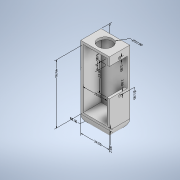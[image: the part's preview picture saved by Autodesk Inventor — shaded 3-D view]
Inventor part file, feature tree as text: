
AUTODESK INVENTOR PART (.ipt)
format: ipt  version: 2022.2 (Build 262287010, 287A)  size: 219,648 bytes
history: native  units: mm
features: other x14, extrude x8, sketch x8, fillet x1
ambient origin geometry x8: Origin, YZ Plane, XZ Plane, XY Plane, X Axis, Y Axis, Z Axis, Center Point
bodies: Solid1 (feature_tree)
feature tree (31):
  other  "Annotations"
  extrude  "Extrusion1"  Depth=24.0mm
  extrude  "Extrusion2"  Depth=2.0mm
  extrude  "Extrusion3"  Depth=15.0mm TaperAngle=0.0deg
  extrude  "Extrusion4"  Depth=2.0mm
  extrude  "Extrusion5"  Depth=8.5mm
  extrude  "Extrusion6"  Depth=3.0mm
  fillet  "Fillet1"  Radius=12.0mm
  extrude  "Extrusion7"  Depth=23.5mm
  extrude  "Extrusion8"  Depth=2.0mm
  sketch  "Sketch1"  dims[d0=24.0mm d1=60.0mm]
  sketch  "Sketch2"  dims[d2=2.0mm d3=0.0mm d4=2.0mm]
  sketch  "Sketch3"  dims[d5=2.0mm d6=15.0mm d7=0.0mm]
  sketch  "Sketch4"  dims[d8=2.0mm d9=2.0mm]
  sketch  "Sketch5"  dims[d10=8.5mm d11=8.5mm]
  sketch  "Sketch6"  dims[d12=27.5mm d13=3.0mm d14=12.0mm d15=0.0mm]
  sketch  "Sketch7"  dims[d23=15.0mm d24=23.5mm]
  sketch  "Sketch8"  dims[d25=2.0mm d26=2.0mm d27=15.0mm d28=0.0mm d29=5.0mm d30=5.0mm d31=0.0mm d32=8.6mm d33=0.0mm d34=10.5mm d35=0.0mm d36=8.5mm d37=2.0mm d38=0.0mm d39=12.0mm d40=12.0mm d41=24.0mm d42=17.0mm d43=8.5mm d44=2.0mm d45=0.0mm d46=53.801048mm d47=6.030652mm d48=3.893802mm d49=8.5mm d50=3.768693mm d51=7.695168mm d52=53.5mm d53=0.0mm d54=10.0mm d55=17.0mm d56=0.0mm d57=10.0mm d58=24.0mm d59=42.144057mm d60=12.0mm d61=0.0mm d62=10.0mm d63=20.0mm d64=0.0mm d65=10.0mm d66=49.5mm d67=4.664241mm d68=4.459377mm d69=23.5mm d70=4.40635mm d71=2.0mm d72=0.553063mm d73=6.890367mm d74=2.0mm d75=61.44687mm d76=2.0mm d77=0.0mm d78=10.0mm d79=5.0mm d80=6.562561mm d81=2.37229mm d82=2.0mm d83=0.5mm d84=0.872665mm d85=0.5mm d86=0.872665mm]
  other  "Radial Dimension 1"
  other  "Linear Dimension 1"
  other  "Linear Dimension 2"
  other  "Linear Dimension 3"
  other  "Diameter Dimension 1"
  other  "Linear Dimension 4"
  other  "Linear Dimension 5"
  other  "Linear Dimension 6"
  other  "Linear Dimension 7"
  other  "Linear Dimension 8"
  other  "Diameter Dimension 2"
  other  "Linear Dimension 9"
  other  "Linear Dimension 10"
